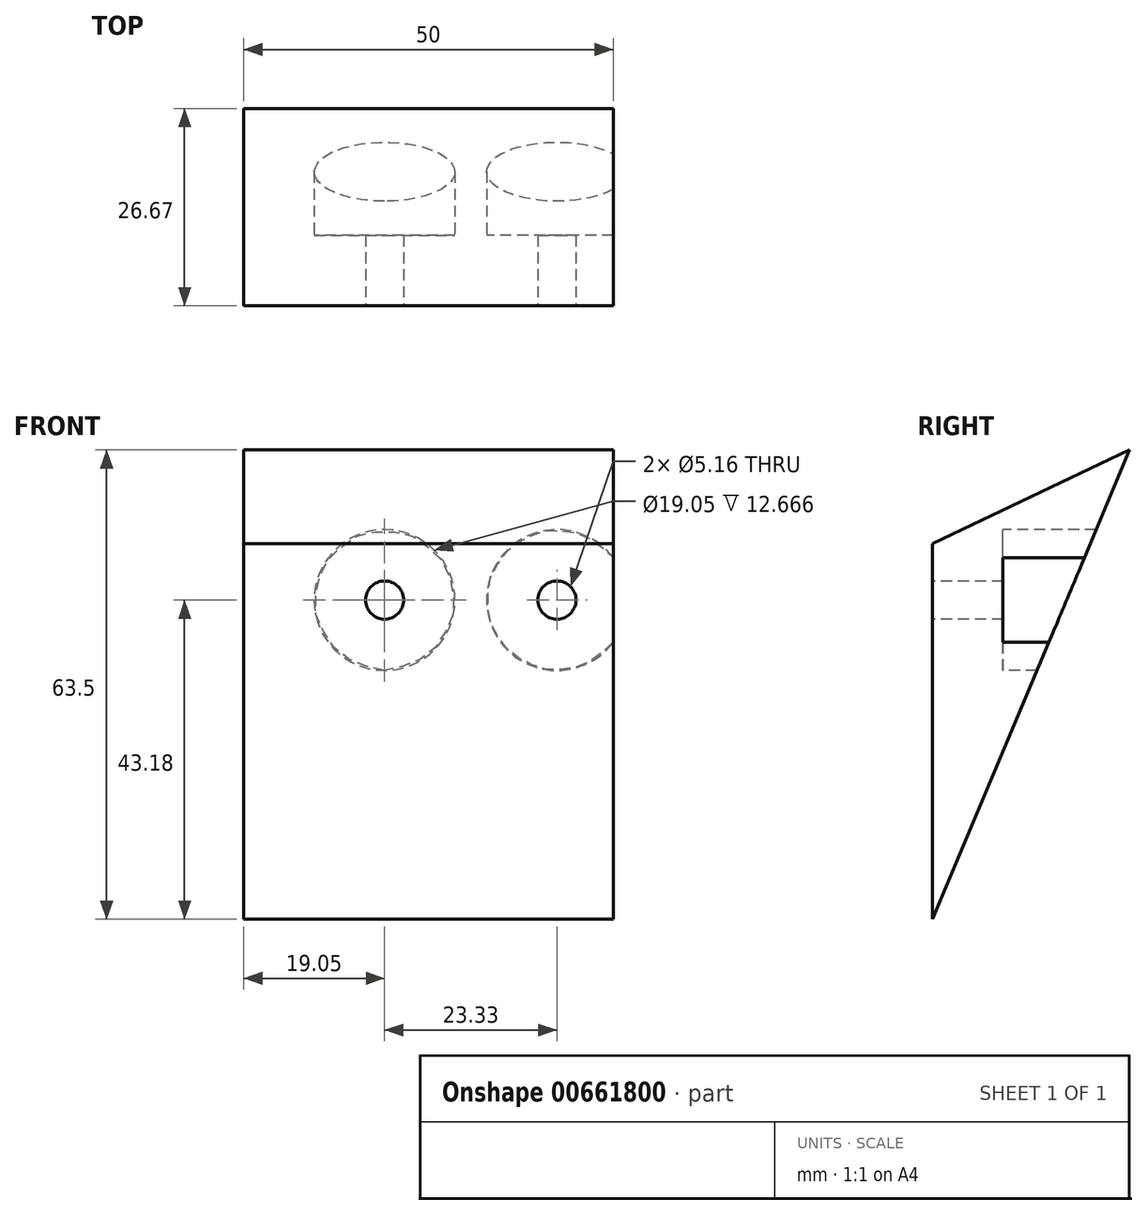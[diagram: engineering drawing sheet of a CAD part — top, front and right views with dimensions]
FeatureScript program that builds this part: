
annotation { "Feature Type Name" : "Feature", "Feature Type Description" : "" }
export const myFeature = defineFeature(function(context is Context, id is Id, definition is map)
    precondition{}
    {
        {
            var Q0;
            Q0=qCreatedBy(makeId("Right.planeOp"),FACE);
            var sketch = newSketch(context, id + "F0", { "sketchPlane" : qUnion([Q0])});
            skLineSegment(sketch, "E0.bottom", {"start": v(-22.12, -25.4) * mm, "end": v(22.12, -25.4) * mm, "construction": true});
            skLineSegment(sketch, "E0.top", {"start": v(-22.12, 25.4) * mm, "end": v(22.12, 25.4) * mm, "construction": true});
            skLineSegment(sketch, "E0.left", {"start": v(-22.12, -25.4) * mm, "end": v(-22.12, 25.4) * mm, "construction": true});
            skLineSegment(sketch, "E0.right", {"start": v(22.12, -25.4) * mm, "end": v(22.12, 25.4) * mm});
            skPoint(sketch, "E0.middle", {"position": v(0, 0) * mm});
            skLineSegment(sketch, "E1", {"start": v(22.12, 25.4) * mm, "end": v(48.8, 38.1) * mm});
            skLineSegment(sketch, "E2", {"start": v(48.8, 38.1) * mm, "end": v(22.12, -25.4) * mm});
            skSolve(sketch);
        }
        {
            var Q0;
            {var subQ0=sQuery(id+"F0.wireOp",EDGE,"E0.right");Q0=makeQuery(id+"F0.imprint","IMPRINT",FACE,{"disambiguationData":[TD([[makeQuery(id+"F0.imprint","IMPRINT",EDGE,{"derivedFrom":subQ0}),-1.0]])]});}
            var Q1;
            {var subQ0=sQuery(id+"F0.wireOp",EDGE,"E1");Q1=makeQuery(id+"F0.imprint","IMPRINT",FACE,{"disambiguationData":[TD([[makeQuery(id+"F0.imprint","IMPRINT",EDGE,{"derivedFrom":subQ0}),-1.0]])]});}
            extrude(context, id + "F1", {"entities" : qUnion([Q0, Q1]), "depth" : 50 * mm, "offsetDistance" : 25.4 * mm});
        }
        {
            var Q0;
            Q0=makeQuery(id+"F1.opExtrude","SWEPT_FACE",FACE,{"disambiguationData":[OSD([sQuery(id+"F0.wireOp",EDGE,"E0.right")])]});
            cPlane(context, id + "F2", {"entities" : qUnion([Q0]), "cplaneType" : CPlaneType.OFFSET, "offset" : 9.52 * mm, "oppositeDirection" : true, "width" : 152.4 * mm, "height" : 152.4 * mm});
        }
        {
            var Q0;
            Q0=qCreatedBy(id+"F2.planeOp",FACE);
            var sketch = newSketch(context, id + "F3", { "sketchPlane" : qUnion([Q0])});
            skLineSegment(sketch, "E3.0", {"start": v(50, 25.4) * mm, "end": v(0, 25.4) * mm});
            skCircle(sketch, "E4", {"center": v(42.38, 17.78) * mm, "radius": 2.58 * mm});
            skCircle(sketch, "E5", {"center": v(19.05, 17.78) * mm, "radius": 2.58 * mm});
            skLineSegment(sketch, "E6.0", {"start": v(50, -25.4) * mm, "end": v(50, 25.4) * mm});
            skSolve(sketch);
        }
        {
            var Q0;
            Q0 = qSketchRegion(id + "F3", true);
            extrude(context, id + "F4", {"entities" : qUnion([Q0]), "operationType" : NewBodyOperationType.REMOVE, "endBound" : BoundingType.THROUGH_ALL, "oppositeDirection" : true, "depth" : 25.4 * mm, "offsetDistance" : 25.4 * mm, "hasSecondDirection" : true, "secondDirectionBound" : SecondDirectionBoundingType.THROUGH_ALL, "secondDirectionOppositeDirection" : false, "secondDirectionDepth" : 25.4 * mm});
        }
        {
            var Q0;
            Q0=qCreatedBy(id+"F2.planeOp",FACE);
            var sketch = newSketch(context, id + "F5", { "sketchPlane" : qUnion([Q0])});
            skCircle(sketch, "E7.0", {"center": v(42.38, 17.78) * mm, "radius": 2.58 * mm});
            skCircle(sketch, "E8.0", {"center": v(19.05, 17.78) * mm, "radius": 2.58 * mm});
            skCircle(sketch, "E9", {"center": v(42.38, 17.78) * mm, "radius": 9.53 * mm});
            skCircle(sketch, "E10", {"center": v(19.05, 17.78) * mm, "radius": 9.53 * mm});
            skLineSegment(sketch, "E11.0", {"start": v(50, 38.1) * mm, "end": v(50, -25.4) * mm});
            skSolve(sketch);
        }
        {
            var Q0;
            Q0 = qSketchRegion(id + "F5", true);
            extrude(context, id + "F6", {"entities" : qUnion([Q0]), "operationType" : NewBodyOperationType.REMOVE, "oppositeDirection" : true, "depth" : 25.4 * mm, "offsetDistance" : 25.4 * mm});
        }
    });
